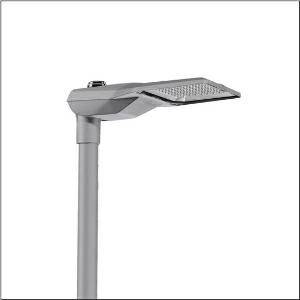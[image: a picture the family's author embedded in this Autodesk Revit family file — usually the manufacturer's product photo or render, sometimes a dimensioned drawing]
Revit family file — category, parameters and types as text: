
# Revit family: streetlight_sl_21_midi___st0_8a_5xe7c47n08nb_23c8
name_source: partatom
category: Lighting Fixtures
units: mm (PartAtom-declared; Revit-internal decimal feet)

## family parameters
Cut with Voids When Loaded = No
Host = Face
Light Source = No
Part Type = Normal
Room Calculation Point = No
Round Connector Dimension = Use Diameter
Shared = No

## types (1)
- --- (1 x LED, 23710 lm, 151.2 W, 4000K)
    Apparent Load = 151 VA
    CIE Flux Codes = 41 75 97 100 100
    Color Rendering = 70
    Color Temperature = 4000K
    Default Elevation = 1800 mm
    Description = Streetlight SL 21 midi, mast luminaire, primary light control with lens, of PMMA, primary optical cover: cover, of toughened safety glass, transparent, light distribution: ST0.8a, light emission: direct distribution, primary light characteristic: asymmetric, installation type: side-entry, LED, 3G 2.5mm², High Power LED, rated luminous flux: 23.710lm, luminous efficacy: 157lm/W, light colour: 740, colour temperature: 4000K, control: overheat protection, presetting dimming linear, constant luminous flux control, time-dependent luminous flux control, flexible luminous flux parameterisation, mains connection: 220..240V, AC, 50/60Hz, connection cable pre-assembled, cable length: 12,5m, wiring characteristics: H05VV-F, start of lifetime: 151W, end of service life: 157W, reduction: 70W, luminaire housing, of diecast aluminium (EN AC-44300), powder-coated, Siteco® metallic grey (DB 702S), corrosivity category C5 mid according to DIN EN ISO 12944, multi-level sealing system, sealing non-destructively replaceable, inclination adjustable: 0°, 5°, 10°, 15°, length: 644mm, width: 335mm, height: 110mm, spigot size: 42mm (side-entry), protection rating (complete): IP66, insulation class (complete): insulation class I (protective earthing), certification: CE, ENEC, ENEC+, VDE, impact resistance: IK09, permissible operating ambient temperature for outdoor applications: -40..+50°C, standard-compliant lighting for roads and squares, packaging unit: 1 piece

Light Distribution: ST0.8a
    Height = 111 mm
    Lamp = 1 x LED
    Lamp Light Flux = 23710 lm
    Lamp Power = 151.2 W
    Lamp count = 1
    Length = 644 mm
    Luminous efficacy = 157 lm/W
    Manufacturer = Siteco
    ModVariant = No
    Model = 5XE7C47N08NB
    Number of Poles = 1
    OnlyDefault = Yes
    Power Factor = 1
    Product Name = Streetlight SL 21 midi | ST0.8a
    Product group = mast luminaire | pylon top
    ProductGroupID = 6100
    Protection Class = Protection class I
    Protection Degree = IP 66
    RLX_Detail_Level = 1
    RLX_Emergency_Light_Flux = 0 lm
    RLX_Emergency_Type = 0
    RLX_Emergency_Type_DB = No
    RlxData = <blob elided: 91621 chars, md5=4c9367c0>
    Socket = socket
    Standby Power = 0 W
    System Light Flux = 23710 lm
    System Power = 151 W
    Type Comments = factory setting: luminous flux: 100 % | dim-lin: 254 | 802 mA
    Type Image = l_1294377.jpg
    URL = http://relux.com
    VarID = @adj_083213
    Voltage = 0 V
    Weight = 0.00 kg
    Width = 336 mm

## geometry (parser evidence)
native form markers: Blend x4, Sweep x11
no freeform markers — native parametric forms only
